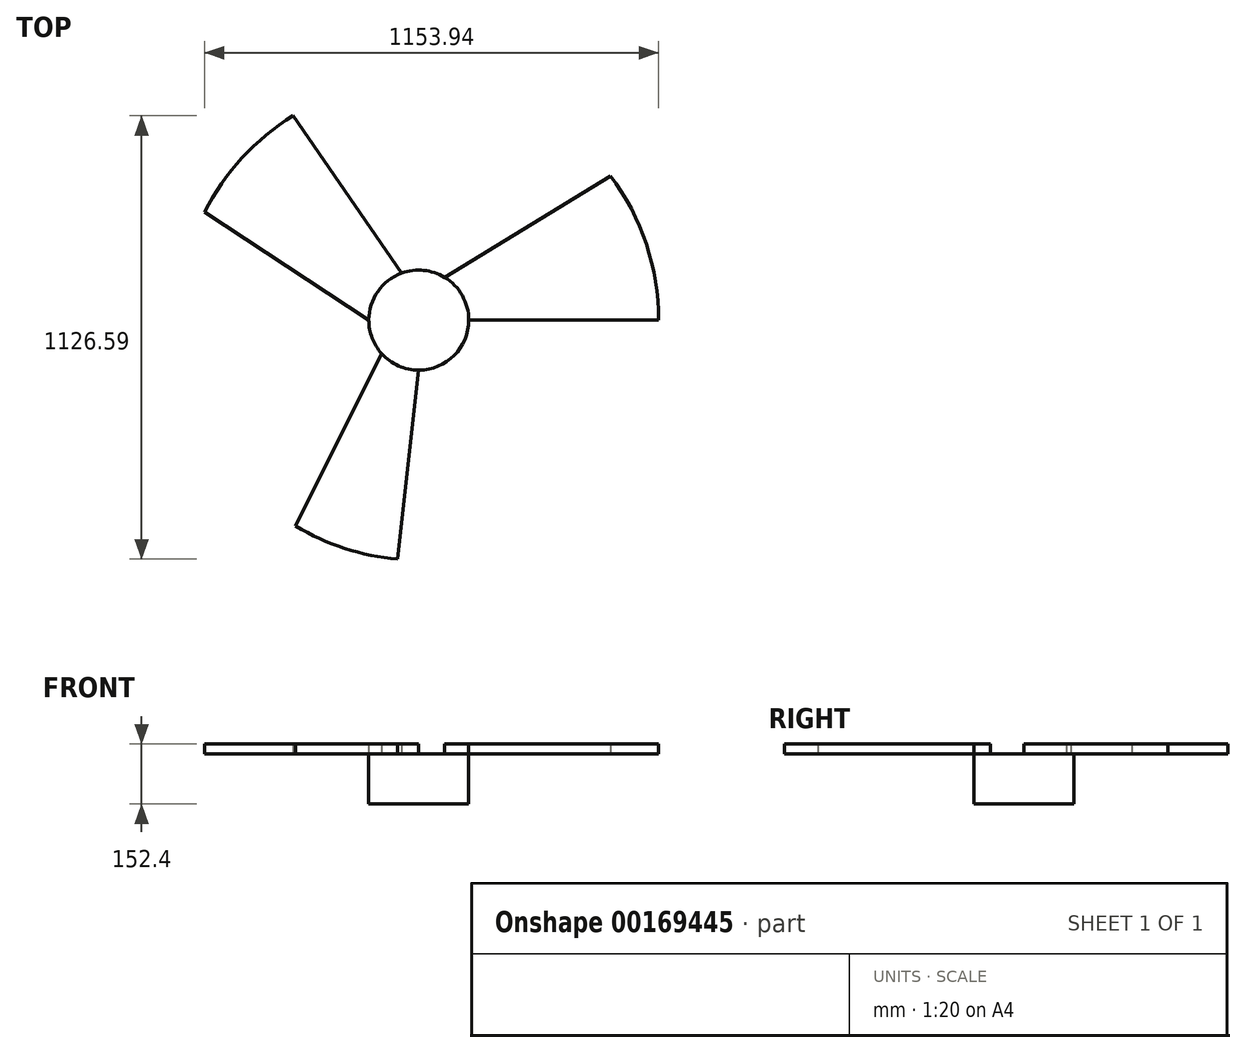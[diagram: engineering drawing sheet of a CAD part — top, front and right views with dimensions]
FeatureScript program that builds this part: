
annotation { "Feature Type Name" : "Feature", "Feature Type Description" : "" }
export const myFeature = defineFeature(function(context is Context, id is Id, definition is map)
    precondition{}
    {
        {
            var Q0;
            Q0=qCreatedBy(makeId("Top.planeOp"),FACE);
            var sketch = newSketch(context, id + "F0", { "sketchPlane" : qUnion([Q0])});
            skCircle(sketch, "E0", {"center": v(0, 0) * mm, "radius": 127 * mm});
            skSolve(sketch);
        }
        {
            var Q0;
            Q0 = qSketchRegion(id + "F0", true);
            extrude(context, id + "F1", {"entities" : qUnion([Q0]), "depth" : 127 * mm});
        }
        {
            var Q0;
            Q0=makeQuery(id+"F1.opExtrude","CAP_FACE",FACE,{"disambiguationData":[OSD([sQuery(id+"F0.wireOp",EDGE,"E0")])],"isStart":false});
            var sketch = newSketch(context, id + "F2", { "sketchPlane" : qUnion([Q0])});
            skCircle(sketch, "E1", {"center": v(0, 0) * mm, "radius": 609.6 * mm});
            skSolve(sketch);
        }
        {
            var Q0;
            Q0 = qSketchRegion(id + "F2", true);
            extrude(context, id + "F3", {"entities" : qUnion([Q0]), "operationType" : NewBodyOperationType.ADD, "depth" : 25.4 * mm});
        }
        {
            var Q0;
            Q0=makeQuery(id+"F3.opExtrude","CAP_FACE",FACE,{"disambiguationData":[OSD([sQuery(id+"F2.wireOp",EDGE,"E1")])],"isStart":true});
            var sketch = newSketch(context, id + "F4", { "sketchPlane" : qUnion([Q0])});
            skArc(sketch, "E2", {"start": v(-94.37, 84.99) * mm, "mid": v(-118.56, 45.52) * mm, "end": v(-127, 0) * mm});
            skLineSegment(sketch, "E3", {"start": v(-94.37, 84.99) * mm, "end": v(-469.26, 835.9) * mm});
            skLineSegment(sketch, "E4", {"start": v(-127, 0) * mm, "end": v(-837.18, -466.97) * mm});
            skCircle(sketch, "E5", {"center": v(0, 0) * mm, "radius": 127 * mm});
            skArc(sketch, "E6", {"start": v(-469.26, 835.9) * mm, "mid": v(-922.53, 260.52) * mm, "end": v(-837.18, -466.97) * mm});
            skLineSegment(sketch, "E7", {"start": v(-43.51, -119.31) * mm, "end": v(-517.39, -807) * mm});
            skLineSegment(sketch, "E8", {"start": v(65.61, -108.74) * mm, "end": v(785.77, -549.09) * mm});
            skLineSegment(sketch, "E9", {"start": v(127, 0) * mm, "end": v(958.61, 0) * mm});
            skLineSegment(sketch, "E10", {"start": v(0, 127) * mm, "end": v(-92.58, 954.13) * mm});
            skArc(sketch, "E11.trimOffspring", {"start": v(958.61, 0) * mm, "mid": v(644.28, 709.82) * mm, "end": v(-92.58, 954.13) * mm});
            skArc(sketch, "E12.trimOffspring", {"start": v(-517.39, -807) * mm, "mid": v(186.1, -940.37) * mm, "end": v(785.77, -549.09) * mm});
            skSolve(sketch);
        }
        {
            var Q0;
            Q0 = qSketchRegion(id + "F4", true);
            extrude(context, id + "F5", {"entities" : qUnion([Q0]), "operationType" : NewBodyOperationType.REMOVE, "oppositeDirection" : true, "depth" : 25.4 * mm});
        }
    });
